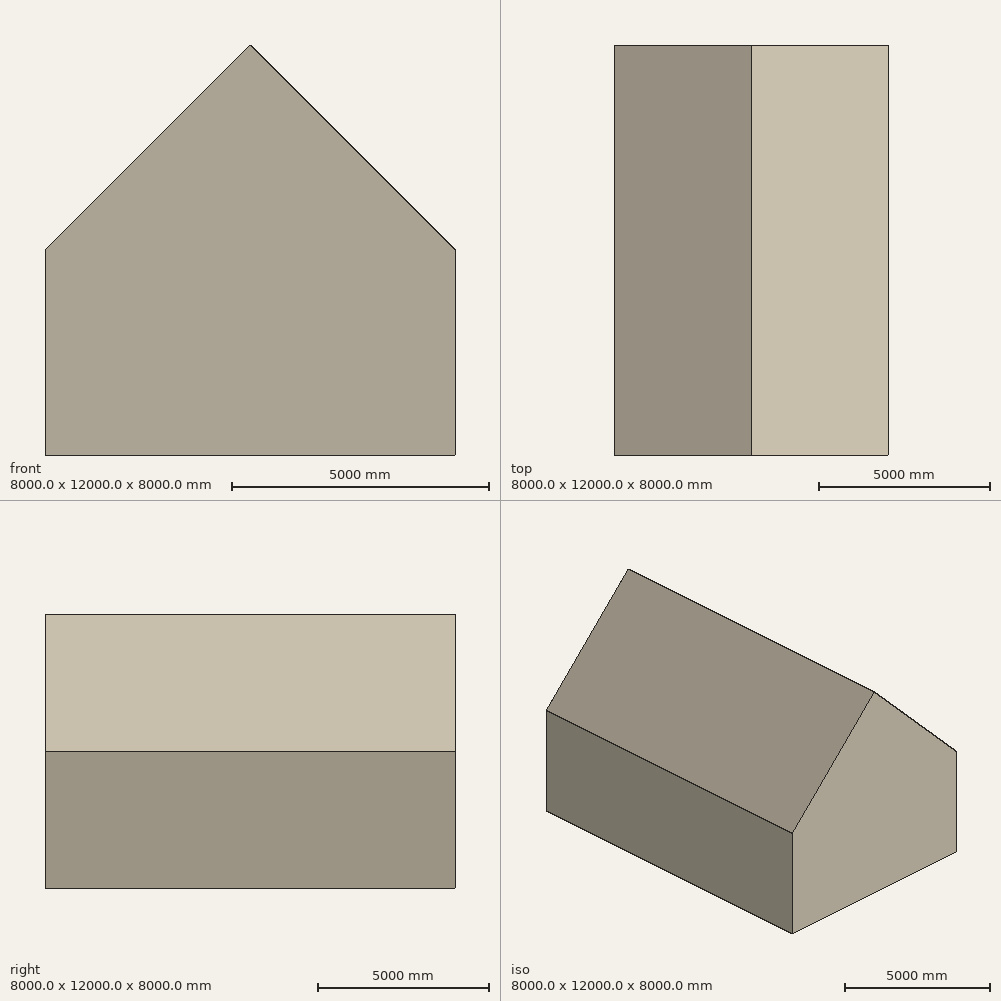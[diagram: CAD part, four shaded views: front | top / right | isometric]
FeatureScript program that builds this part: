
annotation { "Feature Type Name" : "Feature", "Feature Type Description" : "" }
export const myFeature = defineFeature(function(context is Context, id is Id, definition is map)
    precondition{}
    {
        {
            var Q0;
            Q0=qCreatedBy(makeId("Front.planeOp"),FACE);
            var sketch = newSketch(context, id + "F0", { "sketchPlane" : qUnion([Q0])});
            skLineSegment(sketch, "E0.bottom", {"start": v(0, 0) * mm, "end": v(-8000, 0) * mm});
            skLineSegment(sketch, "E0.top", {"start": v(0, 8000) * mm, "end": v(-8000, 8000) * mm});
            skLineSegment(sketch, "E0.left", {"start": v(0, 0) * mm, "end": v(0, 8000) * mm});
            skLineSegment(sketch, "E0.right", {"start": v(-8000, 0) * mm, "end": v(-8000, 8000) * mm});
            skLineSegment(sketch, "E1", {"start": v(0, 4000) * mm, "end": v(-4000, 8000) * mm});
            skLineSegment(sketch, "E2", {"start": v(-4000, 8000) * mm, "end": v(-8000, 4000) * mm});
            skSolve(sketch);
        }
        {
            var Q0;
            Q0=makeQuery(id+"F0.imprint","IMPRINT",FACE,{"disambiguationData":[TD([[makeQuery(id+"F0.imprint","IMPRINT",EDGE,{"derivedFrom":sQuery(id+"F0.wireOp",EDGE,"E0.bottom")}),-1.0]])]});
            extrude(context, id + "F1", {"entities" : qUnion([Q0]), "depth" : 12000 * mm});
        }
    });
